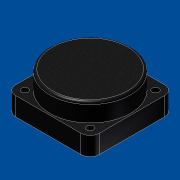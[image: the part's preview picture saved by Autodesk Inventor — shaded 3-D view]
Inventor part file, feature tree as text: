
AUTODESK INVENTOR PART (.ipt)
format: ipt  version: unknown  size: 316,416 bytes
history: native  units: mm
features: sketch x6, plane x5, extrude x4, fillet x2, hole x1, revolve x1, pattern_circular x1, other x1
ambient origin geometry x8: Origin, YZ Plane, XZ Plane, XY Plane, X Axis, Y Axis, Z Axis, Center Point
feature tree (21):
  extrude  "Extrusion1"  Depth=11.0mm TaperAngle=0.0deg
  extrude  "Extrusion2"  Depth=11.0mm TaperAngle=0.0deg
  extrude  "Extrusion3"  Depth=18.0mm TaperAngle=0.0deg
  fillet  "Fillet1"  Radius=1.5mm
  fillet  "Fillet2"  Radius=5.5mm
  hole  "Hole1"  [1 undecoded]
  plane  "Work Plane1"
  extrude  "Extrusion4"  Depth=2.4mm TaperAngle=0.0deg
  plane  "Work Plane2"
  revolve  "Revolution1"  [1 undecoded]
  pattern_circular  "Circular Pattern1"  [2 undecoded]
  sketch  "Sketch1"  dims[d0=50.0mm d1=11.0mm d2=0.0mm]
  sketch  "Sketch2"  dims[d3=48.0mm d4=11.0mm d5=0.0mm]
  sketch  "Sketch3"  dims[d6=40.0mm d7=18.0mm d8=0.0mm d9=1.5mm d10=5.5mm]
  sketch  "Sketch4"  dims[d11=4.0mm d12=6.0mm d13=4.0mm d14=2.0mm d15=90.0deg d16=8.0mm d17=20.594885mm d18=-5.5mm]
  sketch  "Sketch5"  dims[d19=5.5mm d20=2.4mm d21=0.0mm]
  other  "Work Axis1"
  sketch  "Sketch6"  dims[d22=90.0deg d23=4.363323mm d24=4.363323mm d25=2.75mm d26=2.75mm d27=90.0deg d28=40.0mm d29=360.0deg]
  plane  "Work Plane3"
  plane  "Work Plane4"
  plane  "Work Plane5"
note: 4 required parameter values undecoded (feature->parameter linkage not recoverable at this tier; creation-order binding heuristic only, values carry confidence <= 0.55)